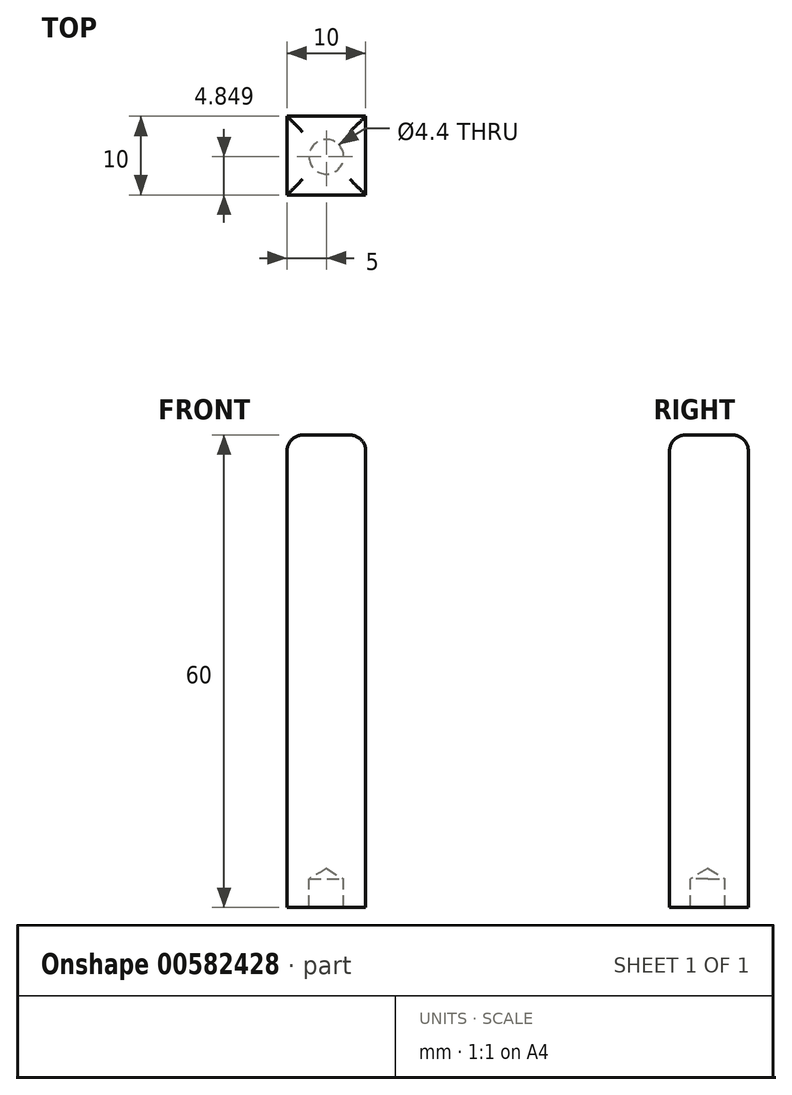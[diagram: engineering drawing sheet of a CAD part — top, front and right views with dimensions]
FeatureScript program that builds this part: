
annotation { "Feature Type Name" : "Feature", "Feature Type Description" : "" }
export const myFeature = defineFeature(function(context is Context, id is Id, definition is map)
    precondition{}
    {
        {
            var Q0;
            Q0=qCreatedBy(makeId("Front.planeOp"),FACE);
            var sketch = newSketch(context, id + "F0", { "sketchPlane" : qUnion([Q0])});
            skLineSegment(sketch, "E0.bottom", {"start": v(-5, 30) * mm, "end": v(5, 30) * mm});
            skLineSegment(sketch, "E0.top", {"start": v(-5, -30) * mm, "end": v(5, -30) * mm});
            skLineSegment(sketch, "E0.left", {"start": v(-5, 30) * mm, "end": v(-5, -30) * mm});
            skLineSegment(sketch, "E0.right", {"start": v(5, 30) * mm, "end": v(5, -30) * mm});
            skPoint(sketch, "E0.middle", {"position": v(0, 0) * mm});
            skSolve(sketch);
        }
        {
            var Q0;
            Q0=makeQuery(id+"F0.imprint","IMPRINT",FACE,{"disambiguationData":[TD([[makeQuery(id+"F0.imprint","IMPRINT",EDGE,{"derivedFrom":sQuery(id+"F0.wireOp",EDGE,"E0.bottom")}),-1.0]])]});
            extrude(context, id + "F1", {"entities" : qUnion([Q0]), "depth" : 10 * mm, "offsetDistance" : 25 * mm});
        }
        {
            var Q0;
            Q0=makeQuery(id+"F1.opExtrude","SWEPT_FACE",FACE,{"disambiguationData":[OSD([sQuery(id+"F0.wireOp",EDGE,"E0.top")])]});
            var sketch = newSketch(context, id + "F2", { "sketchPlane" : qUnion([Q0])});
            skCircle(sketch, "E1", {"center": v(0, 5.15) * mm, "radius": 2.19 * mm});
            skSolve(sketch);
        }
        {
            var Q0;
            Q0=sQuery(id+"F2.wireOp",VERTEX,"E1.center");
            var Q1;
            Q1=makeQuery(id+"F1.opExtrude","SWEPT_BODY",BODY,{"disambiguationData":[OSD([sQuery(id+"F0.wireOp",EDGE,"E0.bottom"),sQuery(id+"F0.wireOp",EDGE,"E0.top"),sQuery(id+"F0.wireOp",EDGE,"E0.left"),sQuery(id+"F0.wireOp",EDGE,"E0.right")])]});
            hole(context, id + "F3", {"style" : HoleStyle.SIMPLE, "endStyle" : HoleEndStyle.BLIND, "holeDiameter" : 4.4 * mm, "majorDiameter" : 5 * mm, "holeDepth" : 3.6 * mm, "isTappedThrough" : true, "tappedDepth" : 12 * mm, "tapClearance" : 3, "locations" : qUnion([Q0]), "scope" : qUnion([Q1])});
        }
        {
            var Q0;
            Q0=makeQuery(id+"F1.opExtrude","SWEPT_FACE",FACE,{"disambiguationData":[OSD([sQuery(id+"F0.wireOp",EDGE,"E0.bottom")])]});
            fillet(context, id + "F4", {"entities" : qUnion([Q0]), "radius" : 2 * mm, "tangentPropagation" : true, "allowEdgeOverflow" : false});
        }
    });
